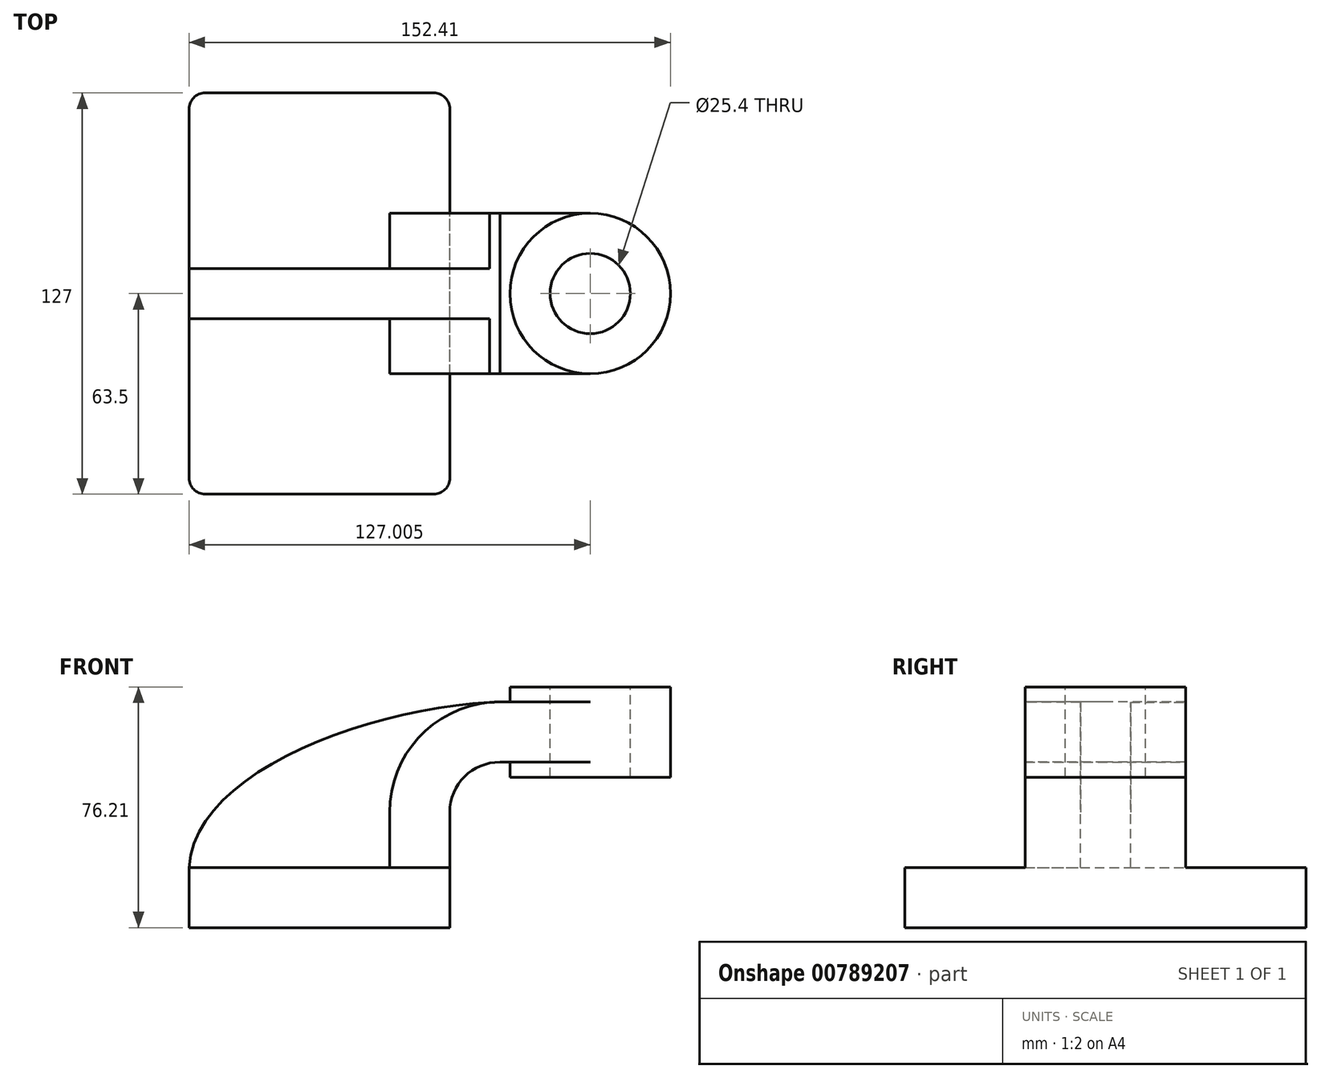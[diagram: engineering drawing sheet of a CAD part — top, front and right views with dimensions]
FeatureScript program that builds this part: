
annotation { "Feature Type Name" : "Feature", "Feature Type Description" : "" }
export const myFeature = defineFeature(function(context is Context, id is Id, definition is map)
    precondition{}
    {
        {
            var Q0;
            Q0=qCreatedBy(makeId("Front.planeOp"),FACE);
            var sketch = newSketch(context, id + "F0", { "sketchPlane" : qUnion([Q0])});
            skLineSegment(sketch, "E0.rect.bottom", {"start": v(-41.28, 9.52) * mm, "end": v(41.28, 9.52) * mm});
            skLineSegment(sketch, "E0.rect.top", {"start": v(-41.28, -9.52) * mm, "end": v(41.28, -9.52) * mm});
            skLineSegment(sketch, "E0.rect.left", {"start": v(-41.28, 9.52) * mm, "end": v(-41.28, -9.52) * mm});
            skLineSegment(sketch, "E0.rect.right", {"start": v(41.28, 9.52) * mm, "end": v(41.28, -9.52) * mm});
            skPoint(sketch, "E0.rect.middle", {"position": v(0, 0) * mm});
            skLineSegment(sketch, "E1", {"start": v(41.28, 9.52) * mm, "end": v(41.28, 27) * mm});
            skArc(sketch, "E2", {"start": v(41.28, 27) * mm, "mid": v(45.92, 38.23) * mm, "end": v(57.15, 42.88) * mm});
            skLineSegment(sketch, "E3", {"start": v(57.15, 42.88) * mm, "end": v(85.72, 42.88) * mm});
            skLineSegment(sketch, "E4.rect.bottom", {"start": v(60.32, 38.1) * mm, "end": v(111.12, 38.1) * mm});
            skLineSegment(sketch, "E4.rect.top", {"start": v(60.32, 66.68) * mm, "end": v(111.12, 66.68) * mm});
            skLineSegment(sketch, "E4.rect.left", {"start": v(60.32, 38.1) * mm, "end": v(60.32, 66.68) * mm});
            skLineSegment(sketch, "E4.rect.right", {"start": v(111.13, 38.1) * mm, "end": v(111.12, 66.68) * mm});
            skPoint(sketch, "E4.rect.middle", {"position": v(85.72, 52.39) * mm});
            skLineSegment(sketch, "E5.0", {"start": v(57.15, 61.93) * mm, "end": v(85.72, 61.93) * mm});
            skArc(sketch, "E5.1", {"start": v(22.23, 27) * mm, "mid": v(32.45, 51.7) * mm, "end": v(57.15, 61.93) * mm});
            skLineSegment(sketch, "E5.2", {"start": v(22.23, 9.52) * mm, "end": v(22.23, 27) * mm});
            skLineSegment(sketch, "E6", {"start": v(85.72, 38.1) * mm, "end": v(85.72, 66.68) * mm});
            skFitSpline(sketch, "E7", {"points": [v(-41.28, 9.53) * mm, v(57.15, 61.93) * mm], "startDerivative": vector(5.2, 92.34) * mm, "endDerivative": vector(120.92, 4.22) * mm});
            skSolve(sketch);
        }
        {
            var Q0;
            Q0=makeQuery(id+"F0.imprint","IMPRINT",FACE,{"disambiguationData":[TD([[makeQuery(id+"F0.imprint","IMPRINT",EDGE,{"derivedFrom":sQuery(id+"F0.wireOp",EDGE,"E0.rect.top")}),1.0]])]});
            extrude(context, id + "F1", {"entities" : qUnion([Q0]), "endBound" : BoundingType.SYMMETRIC, "depth" : 127 * mm});
        }
        {
            var Q0;
            {var subQ9=sQuery(id+"F0.wireOp",EDGE,"E1");Q0=makeQuery(id+"F0.imprint","IMPRINT",FACE,{"disambiguationData":[TD([[makeQuery(id+"F0.imprint","IMPRINT",EDGE,{"derivedFrom":subQ9}),1.0]])]});}
            var Q1;
            {var subQ0=sQuery(id+"F0.wireOp",EDGE,"E6");var subQ1=sQuery(id+"F0.wireOp",EDGE,"E3");var subQ2=makeQuery(id+"F0.imprint","INTERSECT",VERTEX,{"derivedFrom":[subQ1,subQ0]});Q1=makeQuery(id+"F0.imprint","IMPRINT",FACE,{"disambiguationData":[TD([[makeQuery(id+"F0.imprint","IMPRINT",EDGE,{"disambiguationData":[TD([[subQ2,1.0]])],"derivedFrom":subQ1}),1.0]])]});}
            extrude(context, id + "F2", {"entities" : qUnion([Q0, Q1]), "operationType" : NewBodyOperationType.ADD, "endBound" : BoundingType.SYMMETRIC, "depth" : 50.8 * mm});
        }
        {
            var Q0;
            {var subQ3=sQuery(id+"F0.wireOp",EDGE,"E5.2");Q0=makeQuery(id+"F0.imprint","IMPRINT",FACE,{"disambiguationData":[TD([[makeQuery(id+"F0.imprint","IMPRINT",EDGE,{"derivedFrom":subQ3}),1.0]])]});}
            extrude(context, id + "F3", {"entities" : qUnion([Q0]), "operationType" : NewBodyOperationType.ADD, "endBound" : BoundingType.SYMMETRIC, "depth" : 15.88 * mm});
        }
        {
            var Q0;
            {var subQ5=sQuery(id+"F0.wireOp",EDGE,"E4.rect.right");Q0=makeQuery(id+"F0.imprint","IMPRINT",FACE,{"disambiguationData":[TD([[makeQuery(id+"F0.imprint","IMPRINT",EDGE,{"derivedFrom":subQ5}),1.0]])]});}
            var Q1;
            Q1=sQuery(id+"F0.wireOp",EDGE,"E6");
            revolve(context, id + "F4", {"operationType" : NewBodyOperationType.ADD, "entities" : qUnion([Q0]), "axis" : qUnion([Q1]), "revolveType" : RevolveType.FULL});
        }
        {
            var Q0;
            Q0=makeQuery(id+"F1.opExtrude","CAP_EDGE",EDGE,{"disambiguationData":[OSD([sQuery(id+"F0.wireOp",EDGE,"E0.rect.right")])],"isStart":false});
            var Q1;
            Q1=makeQuery(id+"F1.opExtrude","CAP_EDGE",EDGE,{"disambiguationData":[OSD([sQuery(id+"F0.wireOp",EDGE,"E0.rect.left")])],"isStart":false});
            var Q2;
            Q2=makeQuery(id+"F1.opExtrude","CAP_EDGE",EDGE,{"disambiguationData":[OSD([sQuery(id+"F0.wireOp",EDGE,"E0.rect.right")])],"isStart":true});
            var Q3;
            Q3=makeQuery(id+"F1.opExtrude","CAP_EDGE",EDGE,{"disambiguationData":[OSD([sQuery(id+"F0.wireOp",EDGE,"E0.rect.left")])],"isStart":true});
            fillet(context, id + "F5", {"entities" : qUnion([Q0, Q1, Q2, Q3]), "radius" : 5.08 * mm, "tangentPropagation" : true, "allowEdgeOverflow" : false});
        }
        {
            var Q0;
            Q0=makeQuery(id+"F4.opRevolve","SWEPT_FACE",FACE,{"disambiguationData":[OSD([sQuery(id+"F0.wireOp",EDGE,"E4.rect.top")])]});
            var sketch = newSketch(context, id + "F6", { "sketchPlane" : qUnion([Q0])});
            skCircle(sketch, "E8", {"center": v(85.72, 0) * mm, "radius": 12.5 * mm});
            skSolve(sketch);
        }
        {
            var Q0;
            Q0=sQuery(id+"F6.wireOp",VERTEX,"E8.center");
            var Q1;
            Q1=makeQuery(id+"F1.opExtrude","SWEPT_BODY",BODY,{"disambiguationData":[OSD([sQuery(id+"F0.wireOp",EDGE,"E0.rect.bottom"),sQuery(id+"F0.wireOp",EDGE,"E0.rect.top"),sQuery(id+"F0.wireOp",EDGE,"E0.rect.left"),sQuery(id+"F0.wireOp",EDGE,"E0.rect.right")])]});
            hole(context, id + "F7", {"style" : HoleStyle.SIMPLE, "endStyle" : HoleEndStyle.THROUGH, "holeDiameter" : 25.4 * mm, "majorDiameter" : 6.35 * mm, "isTappedThrough" : true, "tappedDepth" : 12.7 * mm, "tapClearance" : 3, "locations" : qUnion([Q0]), "scope" : qUnion([Q1])});
        }
    });
